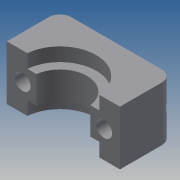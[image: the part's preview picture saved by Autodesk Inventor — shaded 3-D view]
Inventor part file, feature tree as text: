
AUTODESK INVENTOR PART (.ipt)
format: ipt  version: 2013 (Build 170138000, 138)  size: 147,968 bytes
history: native  units: mm
features: extrude x6, sketch x6, fillet x1
ambient origin geometry x8: Origin, YZ Plane, XZ Plane, XY Plane, X Axis, Y Axis, Z Axis, Center Point
bodies: Solid1 (feature_tree)
feature tree (13):
  extrude  "Extrusion1"  Depth=16.0mm
  extrude  "Extrusion2"  Depth=12.0mm
  extrude  "Extrusion3"  Depth=3.0mm TaperAngle=0.0deg
  extrude  "Extrusion4"  Depth=3.0mm TaperAngle=0.0deg
  extrude  "Extrusion5"  Depth=3.5mm
  extrude  "Extrusion6"  Depth=3.0mm TaperAngle=0.0deg
  fillet  "Fillet1"  Radius=6.0mm
  sketch  "Sketch1"  dims[d0=25.0mm d2=16.0mm]
  sketch  "Sketch2"  dims[d3=3.0mm d4=0.0mm d5=12.0mm]
  sketch  "Sketch3"  dims[d7=6.0mm d8=0.0mm d9=3.0mm d10=0.0mm]
  sketch  "Sketch4"  dims[d11=0.75mm d12=3.0mm d13=0.0mm]
  sketch  "Sketch5"  dims[d14=3.5mm d16=3.5mm]
  sketch  "Sketch6"  dims[d17=3.5mm d18=3.0mm d19=0.0mm d20=6.0mm d22=6.0mm d23=3.0mm d24=0.0mm d25=2.5mm]
